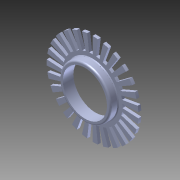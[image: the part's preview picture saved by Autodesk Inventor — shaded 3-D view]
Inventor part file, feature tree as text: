
AUTODESK INVENTOR PART (.ipt)
format: ipt  version: 2011 (Build 150239000, 239)  size: 581,120 bytes
history: native  units: in
note: dims shown in document units (in); Inventor stores cm internally (conversion verified against a paired STEP export)
features: extrude x4, sketch x4, imported_body x1, other x1
ambient origin geometry x8: Origin, YZ Plane, XZ Plane, XY Plane, X Axis, Y Axis, Z Axis, Center Point
feature tree (10):
  imported_body  "Base112"
  extrude  "Extrusion1"  Depth=0.65in
  extrude  "Extrusion2"  Depth=10.6299in TaperAngle=360.0deg
  extrude  "Extrusion3"  Depth=10.6299in TaperAngle=360.0deg
  extrude  "Extrusion4"  Depth=0.042in TaperAngle=0.0deg
  other  "27971 - Motor Mount and Wheel Kit (v1.0)_111"
  sketch  "Sketch1"  dims[d0=1.0in d1=0.0in d2=0.65in]
  sketch  "Sketch2"  dims[d3=0.0458in d4=10.6299in d6=360.0deg]
  sketch  "Sketch3"  dims[d8=0.042in d9=0.0in d10=10.6299in d12=360.0deg]
  sketch  "Sketch4"  dims[d14=0.042in d15=0.0in d16=0.042in d17=0.0in]
